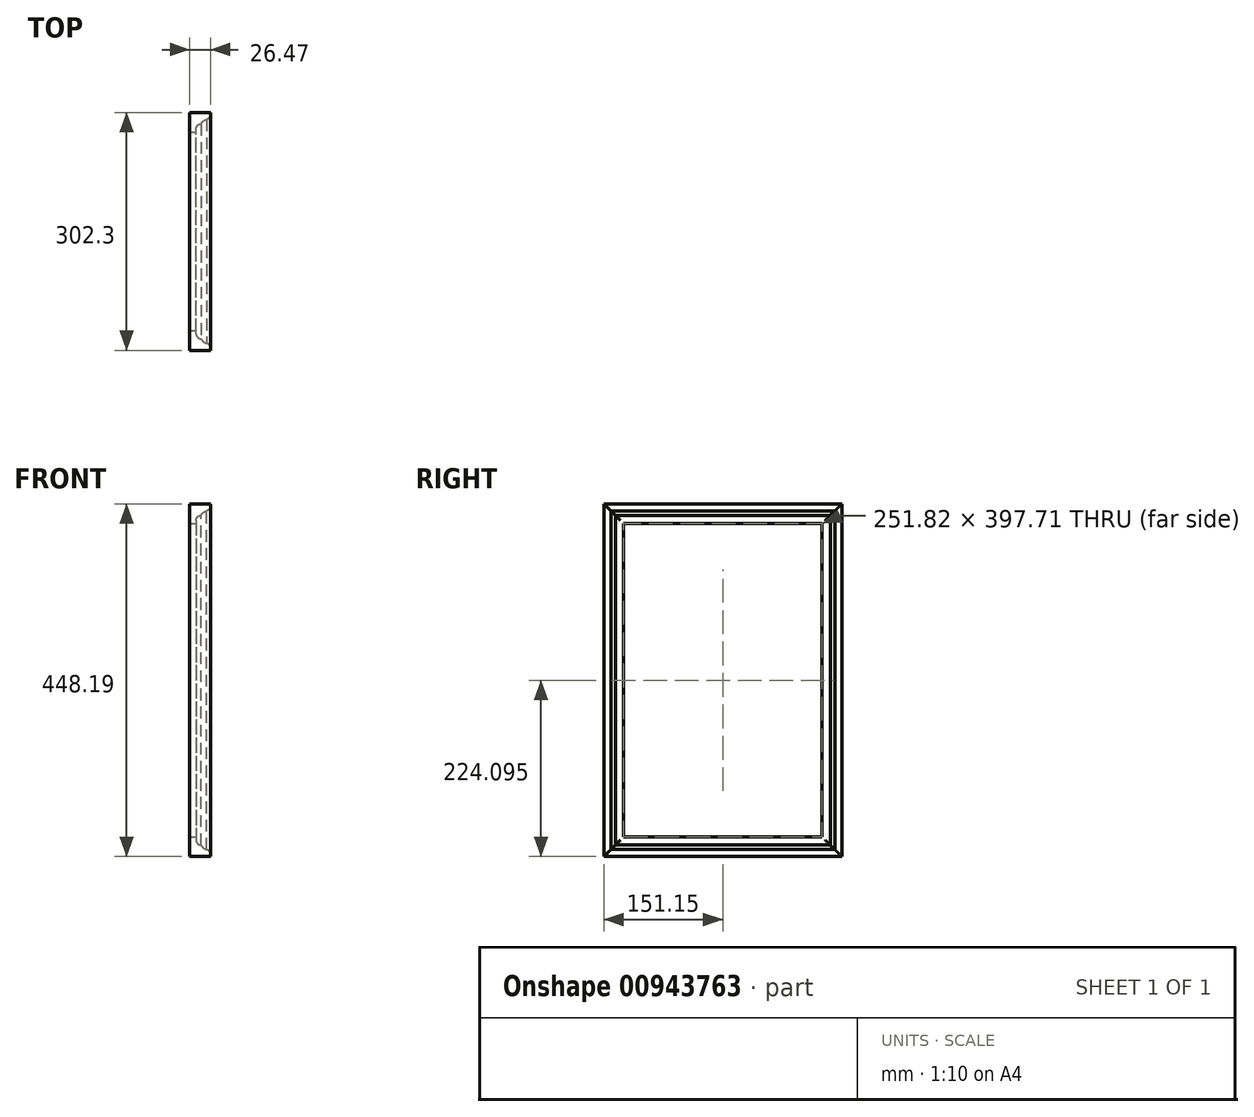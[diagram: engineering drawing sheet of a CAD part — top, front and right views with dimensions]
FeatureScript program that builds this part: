
annotation { "Feature Type Name" : "Feature", "Feature Type Description" : "" }
export const myFeature = defineFeature(function(context is Context, id is Id, definition is map)
    precondition{}
    {
        {
            var Q0;
            Q0=qCreatedBy(makeId("Front.planeOp"),FACE);
            var sketch = newSketch(context, id + "F0", { "sketchPlane" : qUnion([Q0])});
            skLineSegment(sketch, "E0", {"start": v(26.47, 0) * mm, "end": v(0, 0) * mm});
            skLineSegment(sketch, "E1", {"start": v(26.47, 0) * mm, "end": v(26.47, 2.77) * mm});
            skLineSegment(sketch, "E2", {"start": v(14.7, 14.61) * mm, "end": v(14.68, 14.61) * mm});
            skLineSegment(sketch, "E3", {"start": v(8.33, 20.96) * mm, "end": v(8.33, 25.24) * mm});
            skLineSegment(sketch, "E4", {"start": v(8.33, 25.24) * mm, "end": v(0, 25.24) * mm});
            skLineSegment(sketch, "E5", {"start": v(0, 25.24) * mm, "end": v(0, 0) * mm});
            skLineSegment(sketch, "E6", {"start": v(0, 0) * mm, "end": v(26.47, 0) * mm});
            skPoint(sketch, "E7.visualSharp", {"position": v(26.47, 9.31) * mm});
            skArc(sketch, "E7.filletArc", {"start": v(26.47, 2.77) * mm, "mid": v(25.17, 6.61) * mm, "end": v(21.82, 8.89) * mm});
            skArc(sketch, "E8", {"start": v(14.7, 14.61) * mm, "mid": v(17.6, 10.92) * mm, "end": v(21.82, 8.89) * mm});
            skPoint(sketch, "E9.visualSharp", {"position": v(8.33, 14.61) * mm});
            skArc(sketch, "E9.filletArc", {"start": v(8.33, 20.96) * mm, "mid": v(10.2, 16.47) * mm, "end": v(14.68, 14.61) * mm});
            skSolve(sketch);
        }
        {
            var Q0;
            Q0=qCreatedBy(makeId("Right.planeOp"),FACE);
            var sketch = newSketch(context, id + "F1", { "sketchPlane" : qUnion([Q0])});
            skLineSegment(sketch, "E10.bottom", {"start": v(0, 0) * mm, "end": v(-302.3, 0) * mm});
            skLineSegment(sketch, "E10.top", {"start": v(0, 448.19) * mm, "end": v(-302.3, 448.19) * mm});
            skLineSegment(sketch, "E10.left", {"start": v(0, 0) * mm, "end": v(0, 448.19) * mm});
            skLineSegment(sketch, "E10.right", {"start": v(-302.3, 0) * mm, "end": v(-302.3, 448.19) * mm});
            skSolve(sketch);
        }
        {
            var Q0;
            Q0=makeQuery(id+"F0.imprint","IMPRINT",FACE,{"disambiguationData":[TD([[makeQuery(id+"F0.imprint","IMPRINT",EDGE,{"derivedFrom":sQuery(id+"F0.wireOp",EDGE,"E1")}),1.0]])]});
            var Q1;
            Q1=sQuery(id+"F1.wireOp",EDGE,"E10.bottom");
            var Q2;
            Q2=sQuery(id+"F1.wireOp",EDGE,"E10.right");
            var Q3;
            Q3=sQuery(id+"F1.wireOp",EDGE,"E10.top");
            var Q4;
            Q4=sQuery(id+"F1.wireOp",EDGE,"E10.left");
            sweep(context, id + "F2", {"profiles" : qUnion([Q0]), "path" : qUnion([Q1, Q2, Q3, Q4])});
        }
    });
